# Revit family: Seating-LAMMHULTS-PENNE-Armchair
name_source: partatom
category: Furniture
revit_build: Autodesk Revit 2015 (Build: 20160512_0715(x64)
units: mm (PartAtom-declared; Revit-internal decimal feet)

## types (4) — shared parameters
Assembly Code = E2020
Depth = 570 mm  [stored 1.87008 ft]
Description = *Please enter mtrl description here for use in mto*
Height = 790 mm  [stored 2.59186 ft]
Keynote = 46.B
Manufacturer = LAMMHULTS
Model = PENNE
URL = www.lammhults.se
Width = 500 mm  [stored 1.64042 ft]
zero-valued in all types: Length

## per-type parameters (varying)
| type | Armrest Material | Back Material | Frame Material | Seat Material | Weight |
| Platic-Seat | Plastic - Black | Plastic - Black | Colour - Coated - Black | Plastic - Black | 4.4 |
| Plastic-Seat-AluFrame | Plastic - Black | Plastic - Black | Metall - Aluminium - Blank | Plastic - Black | 5.1 |
| Wooden-Seat | Plastic - Black | Wood - Veneer - Ash | Wood - Veneer - Ash | Wood - Veneer - Ash | 3.4 |
| Wooden-Seat-Aluframe | Plastic - White | Wood - Veneer - Oak | Metall - Aluminium - Blank | Wood - Veneer - Oak | 4.1 |

note: [stored X ft] marks values corroborated as IEEE doubles in the binary element streams (Revit-internal decimal feet)

## geometry (parser evidence)
native form markers: Blend x19, Sweep x2
no freeform markers — native parametric forms only
